# Revit family: Interlocked switched 380_415V
name_source: partatom
category: Installations électriques
revit_build: Autodesk Revit 2018 (Build: 20170223_1515(x64)
units: mm (PartAtom-declared; Revit-internal decimal feet)

## family parameters
Conserver l'orientation des annotations = Non
Cote de connecteur circulaire = Utiliser le diamètre
Couper avec des vides une fois chargée = Non
Hôte = Face
Partagée = Non
Point de calcul de pièce = Non
Type d'élément = Normal

## types (4) — shared parameters
Elévation par défaut = 1000 mm  [stored 3.28084 ft]
Fabricant = Legrand
International standard socket for flush mounting or surface mounting with accessory allows the connection of power devices = International standard socket for flush mounting or surface mounting with accessory allows the connection of power devices
Maximum use temperature = +40
Minimum use temperature = -25
Position of earth h = 6
Product family = 0852-P17
Standard IEC or NFC = IEC
Tension V = 400 V  50/60 Hz red
characteristic color = red
connecting type = screw terminals
depth for flush mounting mm = 81 mm  [stored 0.265748 ft]
depth mm = 120 mm  [stored 0.393701 ft]
halogen free = Oui
height mm = 105 mm  [stored 0.344488 ft]
horizontal fixing distance mm = 91 mm
intensity A = 16 A
interlocking type = electrical and mechanical locking
material of box = plastic
vertical fixing distance mm = 87 mm
width mm = 125 mm  [stored 0.410105 ft]

## per-type parameters (varying)
| type | Description | Modèle | Number of poles | protection class IP | resistance to chocks IK |
| P17 - IP55 - 380/415V-16A -3P+N+E | LG-057322_Interlocked switched socket with small flange P17 - IP55 - 380/415V - 16A -3P+E | LG-057322 | 5 | IP55 | 13 |
| P17 - IP55 - 380/415V - 16A -3P+E | LG-057321_Interlocked switched socket with small flange P17 - IP55 - 380/415V - 16A -3P+E | LG-057321 | 4 | IP55 | 12 |
| P17 - IP44 - 380/415V-16A -3P+N+E | LG-057302_Interlocked switched socket with small flange P17 - IP44 - 380/415V - 16A -3P+N+E | LG-057302 | 5 | IP44 | 10 |
| P17 - IP44 - 380/415V - 16A -3P+E | LG-057301_Interlocked switched socket with small flange P17 - IP44 - 380/415V - 16A -3P+E | LG-057301 | 4 | IP44 | 09 |

note: [stored X ft] marks values corroborated as IEEE doubles in the binary element streams (Revit-internal decimal feet)
